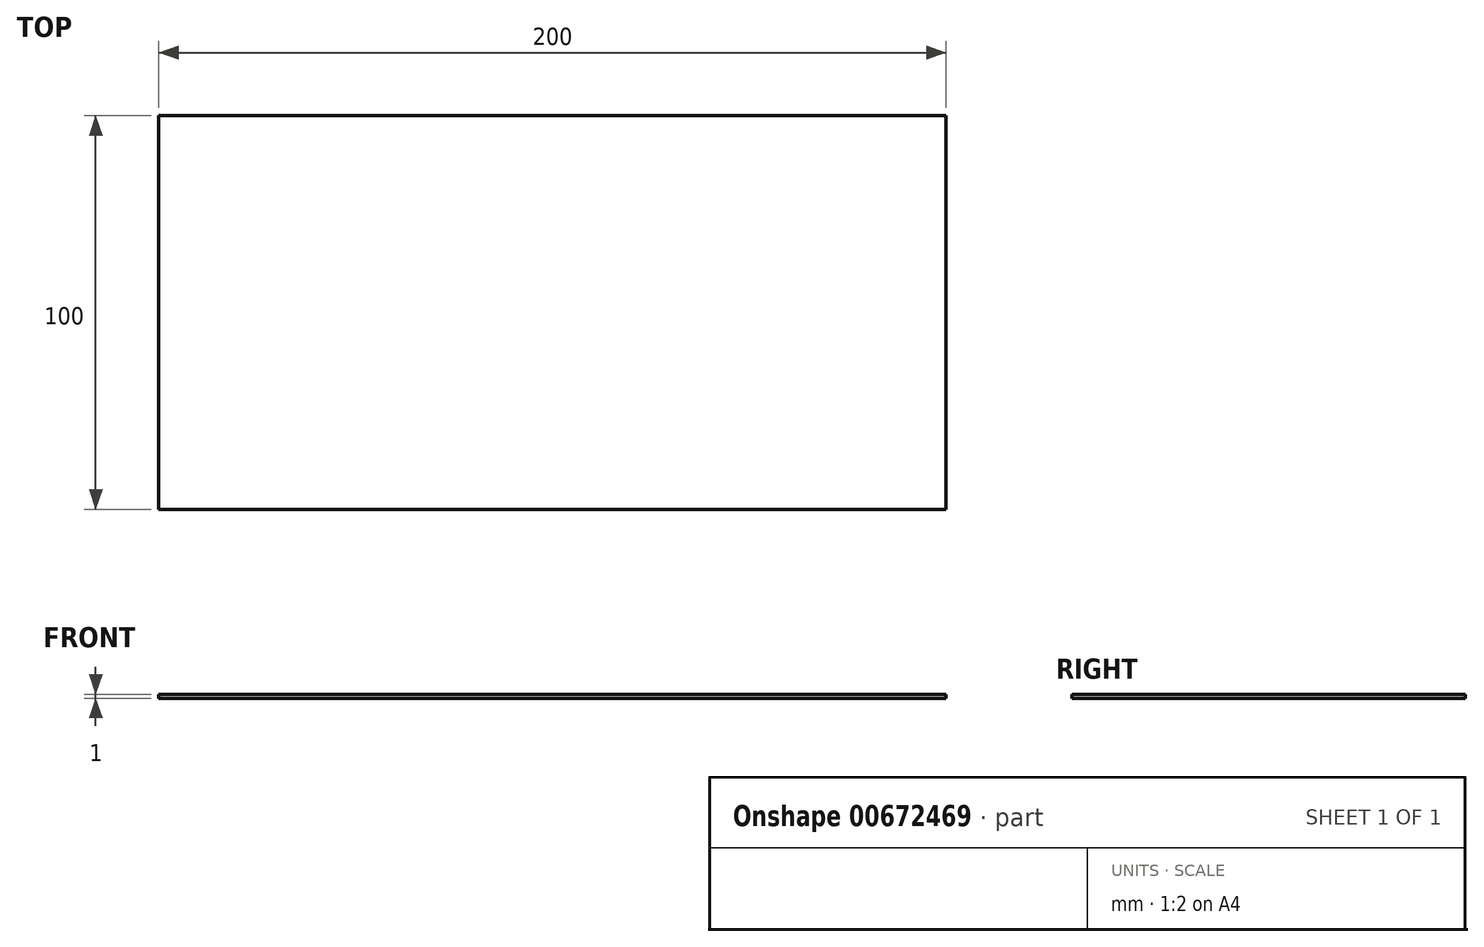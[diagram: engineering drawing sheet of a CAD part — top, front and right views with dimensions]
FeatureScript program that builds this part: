
annotation { "Feature Type Name" : "Feature", "Feature Type Description" : "" }
export const myFeature = defineFeature(function(context is Context, id is Id, definition is map)
    precondition{}
    {
        {
            var Q0;
            Q0=qCreatedBy(makeId("Top.planeOp"),FACE);
            var sketch = newSketch(context, id + "F0", { "sketchPlane" : qUnion([Q0])});
            skLineSegment(sketch, "E0.bottom", {"start": v(100, -50) * mm, "end": v(-100, -50) * mm});
            skLineSegment(sketch, "E0.top", {"start": v(100, 50) * mm, "end": v(-100, 50) * mm});
            skLineSegment(sketch, "E0.left", {"start": v(100, -50) * mm, "end": v(100, 50) * mm});
            skLineSegment(sketch, "E0.right", {"start": v(-100, -50) * mm, "end": v(-100, 50) * mm});
            skPoint(sketch, "E0.middle", {"position": v(0, 0) * mm});
            skSolve(sketch);
        }
        {
            var Q0;
            Q0 = qSketchRegion(id + "F0", true);
            extrude(context, id + "F1", {"entities" : qUnion([Q0]), "depth" : 1 * mm, "offsetDistance" : 25 * mm});
        }
    });
